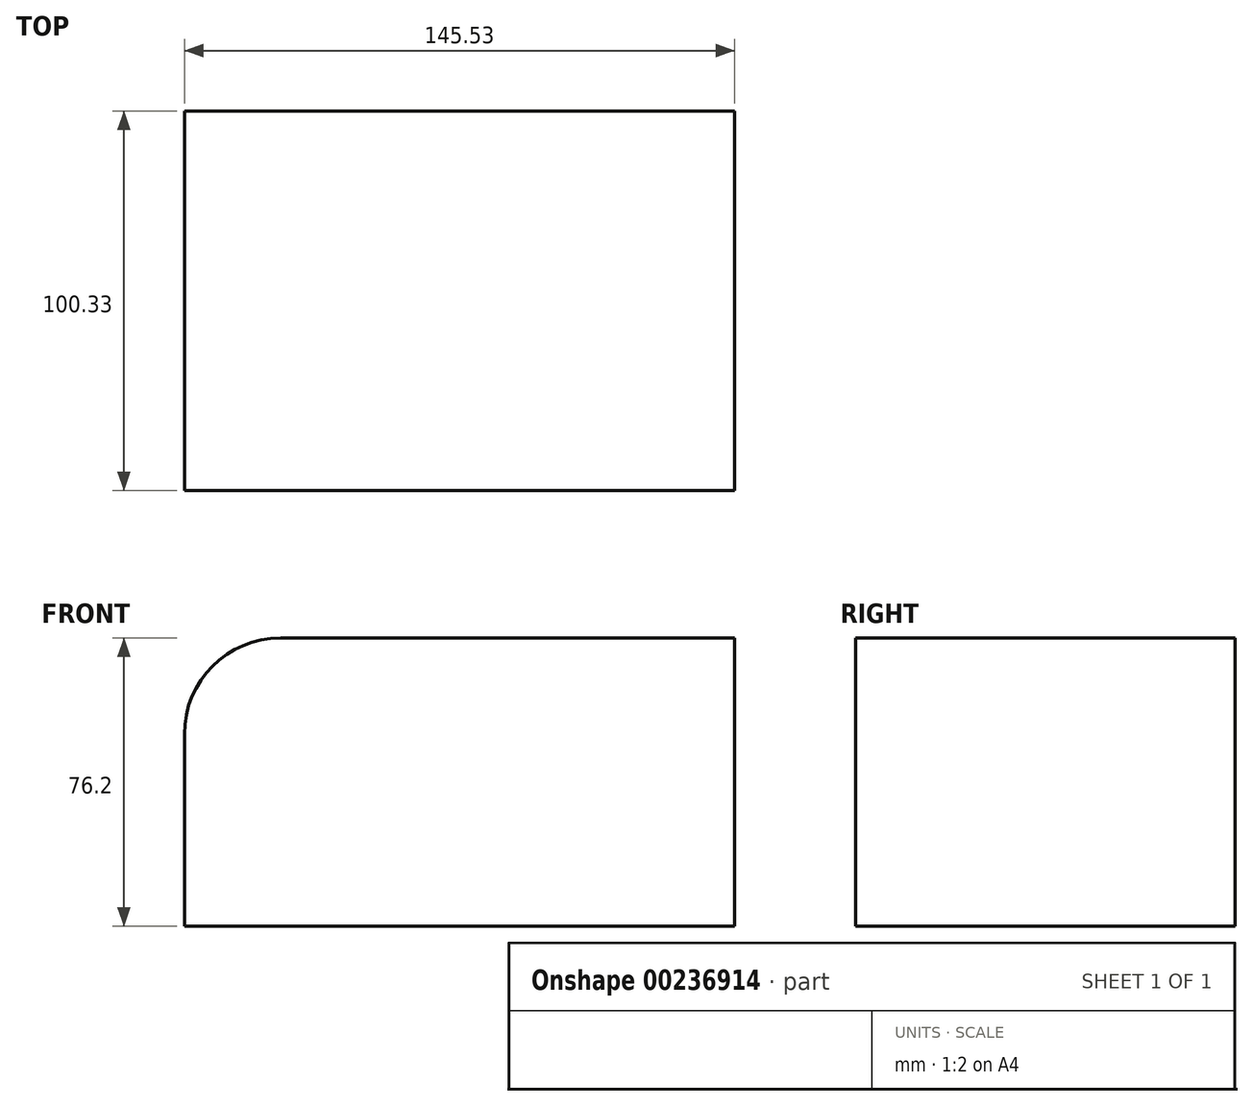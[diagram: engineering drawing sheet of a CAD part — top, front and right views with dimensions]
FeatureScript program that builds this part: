
annotation { "Feature Type Name" : "Feature", "Feature Type Description" : "" }
export const myFeature = defineFeature(function(context is Context, id is Id, definition is map)
    precondition{}
    {
        {
            var Q0;
            Q0=qCreatedBy(makeId("Front.planeOp"),FACE);
            var sketch = newSketch(context, id + "F0", { "sketchPlane" : qUnion([Q0])});
            skLineSegment(sketch, "E0", {"start": v(-48.07, 56.48) * mm, "end": v(44.6, 56.48) * mm});
            skLineSegment(sketch, "E1.bottom", {"start": v(-44.64, 33.83) * mm, "end": v(37.74, 33.83) * mm});
            skLineSegment(sketch, "E1.top", {"start": v(-44.64, 1.56) * mm, "end": v(37.74, 1.56) * mm});
            skLineSegment(sketch, "E1.left", {"start": v(-44.64, 33.83) * mm, "end": v(-44.64, 1.56) * mm});
            skLineSegment(sketch, "E1.right", {"start": v(37.74, 33.83) * mm, "end": v(37.74, 1.56) * mm});
            skLineSegment(sketch, "E2.bottom", {"start": v(-86.17, -16.63) * mm, "end": v(33.96, -16.63) * mm});
            skLineSegment(sketch, "E2.top", {"start": v(-111.57, -92.83) * mm, "end": v(33.96, -92.83) * mm});
            skLineSegment(sketch, "E2.left", {"start": v(-111.57, -42.03) * mm, "end": v(-111.57, -92.83) * mm});
            skLineSegment(sketch, "E2.right", {"start": v(33.96, -16.63) * mm, "end": v(33.96, -92.83) * mm});
            skPoint(sketch, "E2.middle", {"position": v(-38.8, -54.73) * mm});
            skCircle(sketch, "E3", {"center": v(-118.78, 49.62) * mm, "radius": 32.6 * mm});
            skFitSpline(sketch, "E4", {"points": [v(-81.71, 93.21) * mm, v(-68.67, 94.58) * mm, v(-32.97, 113.46) * mm, v(-1.4, 105.22) * mm, v(8.56, 91.5) * mm, v(43.57, 105.57) * mm, v(73.78, 94.58) * mm, v(71.72, 62.66) * mm, v(90.6, 34.86) * mm], "startDerivative": vector(140.36, -14.24) * mm, "endDerivative": vector(198.96, -190.03) * mm});
            skLineSegment(sketch, "E5.MirrorCS", {"start": v(-44.64, 79.14) * mm, "end": v(37.74, 79.14) * mm});
            skLineSegment(sketch, "E6.MirrorCS", {"start": v(-44.64, 111.4) * mm, "end": v(37.74, 111.4) * mm});
            skLineSegment(sketch, "E7.MirrorCS", {"start": v(37.74, 79.14) * mm, "end": v(37.74, 111.4) * mm});
            skLineSegment(sketch, "E8.MirrorCS", {"start": v(-44.64, 79.14) * mm, "end": v(-44.64, 111.4) * mm});
            skCircle(sketch, "E9.MirrorC", {"center": v(-118.78, 63.35) * mm, "radius": 32.6 * mm});
            skPoint(sketch, "E10.visualSharp", {"position": v(-111.57, -16.63) * mm});
            skArc(sketch, "E10.filletArc", {"start": v(-86.17, -16.63) * mm, "mid": v(-104.13, -24.07) * mm, "end": v(-111.57, -42.03) * mm});
            skSolve(sketch);
        }
        {
            var Q0;
            Q0=makeQuery(id+"F0.imprint","IMPRINT",FACE,{"disambiguationData":[TD([[makeQuery(id+"F0.imprint","IMPRINT",EDGE,{"derivedFrom":sQuery(id+"F0.wireOp",EDGE,"E2.bottom")}),-1.0]])]});
            extrude(context, id + "F1", {"entities" : qUnion([Q0]), "oppositeDirection" : true, "depth" : 100.33 * mm});
        }
    });
